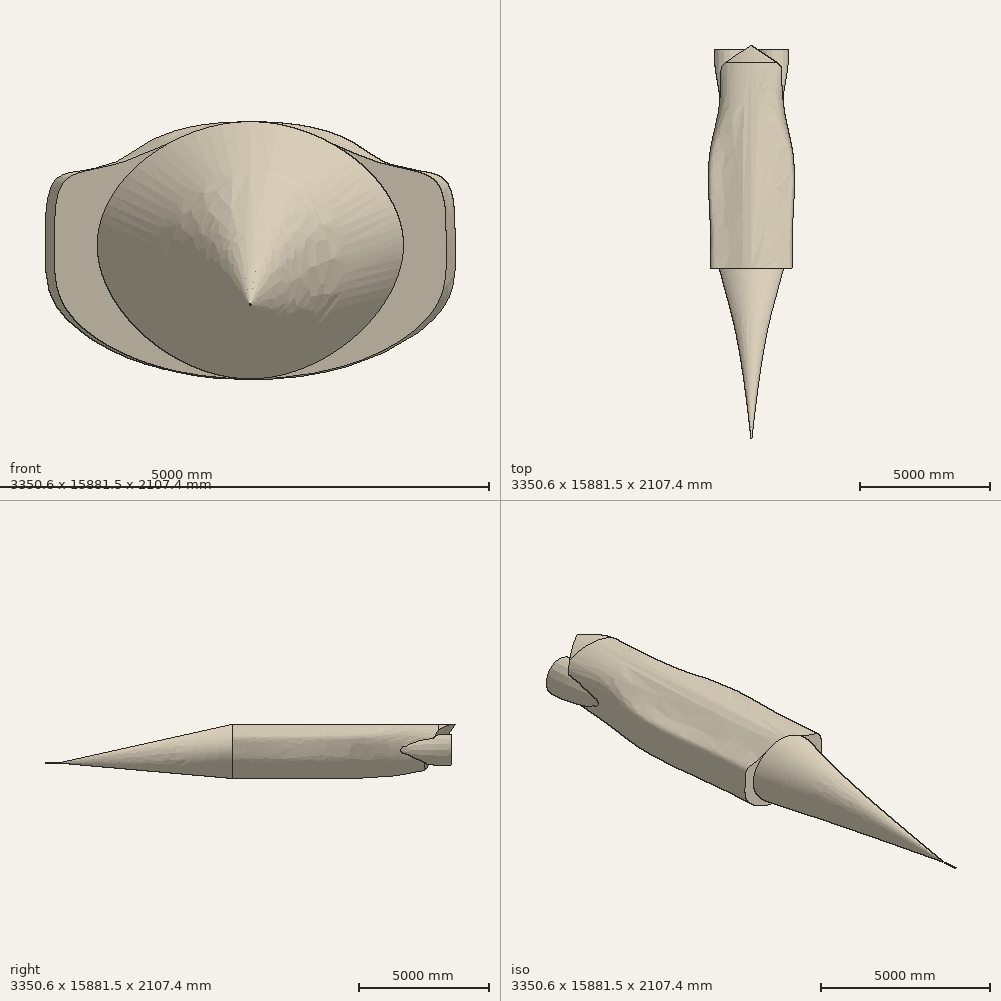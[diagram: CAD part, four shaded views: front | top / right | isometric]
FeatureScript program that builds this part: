
annotation { "Feature Type Name" : "Feature", "Feature Type Description" : "" }
export const myFeature = defineFeature(function(context is Context, id is Id, definition is map)
    precondition{}
    {
        {
            var Q0;
            Q0=qCreatedBy(makeId("Front.planeOp"),FACE);
            cPlane(context, id + "F0", {"entities" : qUnion([Q0]), "cplaneType" : CPlaneType.OFFSET, "offset" : 1750 * mm, "width" : 152.4 * mm, "height" : 152.4 * mm});
        }
        {
            var Q0;
            Q0=qCreatedBy(id+"F0.planeOp",FACE);
            var sketch = newSketch(context, id + "F1", { "sketchPlane" : qUnion([Q0])});
            skPoint(sketch, "E0.middle", {"position": v(0, 0) * mm});
            skFitSpline(sketch, "E1", {"points": [v(0, 1000) * mm, v(-1060, 662.5) * mm, v(-1517.6, 506.84) * mm, v(-1600, 0) * mm, v(-1517.6, -506.84) * mm, v(-750, -1000) * mm, v(750, -1000) * mm, v(1517.6, -506.84) * mm, v(1600, 0) * mm, v(1517.6, 506.84) * mm, v(1060, 662.5) * mm, v(0, 1000) * mm]});
            skSolve(sketch);
        }
        {
            var Q0;
            Q0=qCreatedBy(makeId("Front.planeOp"),FACE);
            var sketch = newSketch(context, id + "F2", { "sketchPlane" : qUnion([Q0])});
            skPoint(sketch, "E2.middle", {"position": v(0, 0) * mm});
            skFitSpline(sketch, "E3", {"points": [v(0, 1000) * mm, v(-1060, 662.5) * mm, v(-1517.6, 506.84) * mm, v(-1600, 0) * mm, v(-1517.6, -506.84) * mm, v(-750, -1000) * mm, v(750, -1000) * mm, v(1517.6, -506.84) * mm, v(1600, 0) * mm, v(1517.6, 506.84) * mm, v(1060, 662.5) * mm, v(0, 1000) * mm]});
            skSolve(sketch);
        }
        {
            var Q0;
            Q0=qCreatedBy(makeId("Front.planeOp"),FACE);
            cPlane(context, id + "F3", {"entities" : qUnion([Q0]), "cplaneType" : CPlaneType.OFFSET, "offset" : 2800 * mm, "oppositeDirection" : true, "width" : 150 * mm, "height" : 150 * mm});
        }
        {
            var Q0;
            Q0=qCreatedBy(id+"F3.planeOp",FACE);
            var sketch = newSketch(context, id + "F4", { "sketchPlane" : qUnion([Q0])});
            skPoint(sketch, "E4.middle", {"position": v(0, 0) * mm});
            skFitSpline(sketch, "E5", {"points": [v(0, 1000) * mm, v(-1060, 662.5) * mm, v(-1517.6, 506.84) * mm, v(-1600, 0) * mm, v(-1517.6, -506.84) * mm, v(-750, -1000) * mm, v(750, -1000) * mm, v(1517.6, -506.84) * mm, v(1600, 0) * mm, v(1517.6, 506.84) * mm, v(1060, 662.5) * mm, v(0, 1000) * mm]});
            skSolve(sketch);
        }
        {
            var Q0;
            Q0=qCreatedBy(makeId("Front.planeOp"),FACE);
            cPlane(context, id + "F5", {"entities" : qUnion([Q0]), "cplaneType" : CPlaneType.OFFSET, "offset" : 4500 * mm, "oppositeDirection" : true, "width" : 150 * mm, "height" : 150 * mm});
        }
        {
            var Q0;
            Q0=qCreatedBy(id+"F5.planeOp",FACE);
            var sketch = newSketch(context, id + "F6", { "sketchPlane" : qUnion([Q0])});
            skPoint(sketch, "E6.middle", {"position": v(0, 0) * mm});
            skFitSpline(sketch, "E7", {"points": [v(0, 1000) * mm, v(-1060, 662.5) * mm, v(-1250, 0) * mm, v(-1060, -662.5) * mm, v(0, -1000) * mm, v(1060, -662.5) * mm, v(1250, 0) * mm, v(1060, 662.5) * mm, v(0, 1000) * mm]});
            skSolve(sketch);
        }
        {
            var Q0;
            Q0=qCreatedBy(makeId("Front.planeOp"),FACE);
            cPlane(context, id + "F7", {"entities" : qUnion([Q0]), "cplaneType" : CPlaneType.OFFSET, "offset" : 6232.05 * mm, "oppositeDirection" : true, "width" : 150 * mm, "height" : 150 * mm});
        }
        {
            var Q0;
            Q0=qCreatedBy(id+"F7.planeOp",FACE);
            var sketch = newSketch(context, id + "F8", { "sketchPlane" : qUnion([Q0])});
            skPoint(sketch, "E8.middle", {"position": v(0, 0) * mm});
            skFitSpline(sketch, "E9", {"points": [v(0, 1000) * mm, v(-1060, 662.5) * mm, v(-1250, 0) * mm, v(-848, -530) * mm, v(848, -530) * mm, v(1250, 0) * mm, v(1060, 662.5) * mm, v(0, 1000) * mm]});
            skSolve(sketch);
        }
        {
            var Q0;
            Q0=makeQuery(id+"F1.imprint","IMPRINT",FACE,{"disambiguationData":[TD([[makeQuery(id+"F1.imprint","IMPRINT",EDGE,{"derivedFrom":sQuery(id+"F1.wireOp",EDGE,"E1")}),1.0]])]});
            var Q1;
            Q1=makeQuery(id+"F2.imprint","IMPRINT",FACE,{"disambiguationData":[TD([[makeQuery(id+"F2.imprint","IMPRINT",EDGE,{"derivedFrom":sQuery(id+"F2.wireOp",EDGE,"E3")}),1.0]])]});
            var Q2;
            Q2=makeQuery(id+"F4.imprint","IMPRINT",FACE,{"disambiguationData":[TD([[makeQuery(id+"F4.imprint","IMPRINT",EDGE,{"derivedFrom":sQuery(id+"F4.wireOp",EDGE,"E5")}),1.0]])]});
            var Q3;
            Q3=makeQuery(id+"F6.imprint","IMPRINT",FACE,{"disambiguationData":[TD([[makeQuery(id+"F6.imprint","IMPRINT",EDGE,{"derivedFrom":sQuery(id+"F6.wireOp",EDGE,"E7")}),1.0]])]});
            var Q4;
            Q4=makeQuery(id+"F8.imprint","IMPRINT",FACE,{"disambiguationData":[TD([[makeQuery(id+"F8.imprint","IMPRINT",EDGE,{"derivedFrom":sQuery(id+"F8.wireOp",EDGE,"E9")}),1.0]])]});
            loft(context, id + "F9", {"sheetProfilesArray" : [{ "sheetProfileEntities" : qUnion([Q0]) }, { "sheetProfileEntities" : qUnion([Q1]) }, { "sheetProfileEntities" : qUnion([Q2]) }, { "sheetProfileEntities" : qUnion([Q3]) }, { "sheetProfileEntities" : qUnion([Q4]) }]});
        }
        {
            var Q0;
            Q0=makeQuery(id+"F9.opLoft","CAP_FACE",FACE,{"disambiguationData":[OSD([makeQuery(id+"F8.imprint","IMPRINT",FACE,{"disambiguationData":[TD([[makeQuery(id+"F8.imprint","IMPRINT",EDGE,{"derivedFrom":sQuery(id+"F8.wireOp",EDGE,"E9")}),1.0]])]})])],"isStart":true});
            extrude(context, id + "F10", {"entities" : qUnion([Q0]), "operationType" : NewBodyOperationType.ADD, "depth" : 649.4 * mm, "offsetDistance" : 25 * mm});
        }
        {
            var Q0;
            Q0=qCreatedBy(makeId("Right.planeOp"),FACE);
            var sketch = newSketch(context, id + "F11", { "sketchPlane" : qUnion([Q0])});
            skLineSegment(sketch, "E10", {"start": v(0, 0) * mm, "end": v(4500, 0) * mm});
            skLineSegment(sketch, "E11", {"start": v(4500, 0) * mm, "end": v(6232.05, 0) * mm});
            skLineSegment(sketch, "E12", {"start": v(4500, 0) * mm, "end": v(4500, 1000) * mm});
            skLineSegment(sketch, "E13", {"start": v(4500, 1000) * mm, "end": v(6881.46, 1000) * mm});
            skLineSegment(sketch, "E14", {"start": v(6881.46, 1000) * mm, "end": v(6881.46, -1000) * mm});
            skLineSegment(sketch, "E15", {"start": v(6881.46, 1000) * mm, "end": v(6232.05, 0) * mm});
            skLineSegment(sketch, "E16", {"start": v(6232.05, 0) * mm, "end": v(5582.64, -1000) * mm});
            skLineSegment(sketch, "E17", {"start": v(5582.64, -1000) * mm, "end": v(6881.46, -1000) * mm});
            skSolve(sketch);
        }
        {
            var Q0;
            Q0=makeQuery(id+"F11.imprint","IMPRINT",FACE,{"disambiguationData":[TD([[makeQuery(id+"F11.imprint","IMPRINT",EDGE,{"derivedFrom":sQuery(id+"F11.wireOp",EDGE,"E14")}),-1.0]])]});
            var Q1;
            Q1=sQuery(id+"F11.wireOp",EDGE,"E13");
            revolve(context, id + "F12", {"operationType" : NewBodyOperationType.REMOVE, "entities" : qUnion([Q0]), "axis" : qUnion([Q1]), "revolveType" : RevolveType.SYMMETRIC, "oppositeDirection" : true, "angle" : 182 * degree});
        }
        {
            var Q0;
            Q0=qCreatedBy(id+"F0.planeOp",FACE);
            var sketch = newSketch(context, id + "F13", { "sketchPlane" : qUnion([Q0])});
            skFitSpline(sketch, "E18", {"points": [v(0, 1000) * mm, v(-1250, 0) * mm, v(0, -1099.92) * mm, v(1250, 0) * mm, v(0, 1000) * mm]});
            skSolve(sketch);
        }
        {
            var Q0;
            Q0=qCreatedBy(makeId("Front.planeOp"),FACE);
            cPlane(context, id + "F14", {"entities" : qUnion([Q0]), "cplaneType" : CPlaneType.OFFSET, "offset" : 3500 * mm, "width" : 150 * mm, "height" : 150 * mm});
        }
        {
            var Q0;
            Q0=qCreatedBy(id+"F14.planeOp",FACE);
            var sketch = newSketch(context, id + "F15", { "sketchPlane" : qUnion([Q0])});
            skCircle(sketch, "E19", {"center": v(0, -166.46) * mm, "radius": 777.75 * mm});
            skSolve(sketch);
        }
        {
            var Q0;
            Q0=qCreatedBy(makeId("Front.planeOp"),FACE);
            cPlane(context, id + "F16", {"entities" : qUnion([Q0]), "cplaneType" : CPlaneType.OFFSET, "offset" : 8450 * mm, "width" : 150 * mm, "height" : 150 * mm});
        }
        {
            var Q0;
            Q0=qCreatedBy(id+"F16.planeOp",FACE);
            var sketch = newSketch(context, id + "F17", { "sketchPlane" : qUnion([Q0])});
            skCircle(sketch, "E20", {"center": v(0, -495.98) * mm, "radius": 7.78 * mm});
            skSolve(sketch);
        }
        {
            var Q1;
            Q1=makeQuery(id+"F13.imprint","IMPRINT",FACE,{"disambiguationData":[TD([[makeQuery(id+"F13.imprint","IMPRINT",EDGE,{"derivedFrom":sQuery(id+"F13.wireOp",EDGE,"E18")}),1.0]])]});
            var Q2;
            Q2=makeQuery(id+"F15.imprint","IMPRINT",FACE,{"disambiguationData":[TD([[makeQuery(id+"F15.imprint","IMPRINT",EDGE,{"derivedFrom":sQuery(id+"F15.wireOp",EDGE,"E19")}),1.0]])]});
            var Q3;
            Q3=makeQuery(id+"F17.imprint","IMPRINT",FACE,{"disambiguationData":[TD([[makeQuery(id+"F17.imprint","IMPRINT",EDGE,{"derivedFrom":sQuery(id+"F17.wireOp",EDGE,"E20")}),1.0]])]});
            loft(context, id + "F18", {"operationType" : NewBodyOperationType.ADD, "sheetProfilesArray" : [{ "sheetProfileEntities" : qUnion([Q1]) }, { "sheetProfileEntities" : qUnion([Q2]) }, { "sheetProfileEntities" : qUnion([Q3]) }]});
        }
        {
            var Q0;
            Q0=makeQuery(id+"F18.opLoft","CAP_FACE",FACE,{"disambiguationData":[OSD([makeQuery(id+"F17.imprint","IMPRINT",FACE,{"disambiguationData":[TD([[makeQuery(id+"F17.imprint","IMPRINT",EDGE,{"derivedFrom":sQuery(id+"F17.wireOp",EDGE,"E20")}),1.0]])]})])],"isStart":true});
            extrude(context, id + "F19", {"entities" : qUnion([Q0]), "operationType" : NewBodyOperationType.ADD, "depth" : 550 * mm, "offsetDistance" : 25 * mm});
        }
        {
            var Q0;
            Q0=qCreatedBy(makeId("Front.planeOp"),FACE);
            cPlane(context, id + "F20", {"entities" : qUnion([Q0]), "cplaneType" : CPlaneType.OFFSET, "offset" : 3500 * mm, "oppositeDirection" : true, "width" : 150 * mm, "height" : 150 * mm});
        }
        {
            var Q0;
            Q0=qCreatedBy(id+"F20.planeOp",FACE);
            var sketch = newSketch(context, id + "F21", { "sketchPlane" : qUnion([Q0])});
            skCircle(sketch, "E21", {"center": v(-825, 0) * mm, "radius": 600 * mm});
            skCircle(sketch, "E22", {"center": v(825, 0) * mm, "radius": 600 * mm});
            skSolve(sketch);
        }
        {
            var Q0;
            Q0=qCreatedBy(makeId("Front.planeOp"),FACE);
            cPlane(context, id + "F22", {"entities" : qUnion([Q0]), "cplaneType" : CPlaneType.OFFSET, "offset" : 4500 * mm, "oppositeDirection" : true, "width" : 150 * mm, "height" : 150 * mm});
        }
        {
            var Q0;
            Q0=qCreatedBy(id+"F22.planeOp",FACE);
            var sketch = newSketch(context, id + "F23", { "sketchPlane" : qUnion([Q0])});
            skCircle(sketch, "E23", {"center": v(-825, 0) * mm, "radius": 400 * mm});
            skCircle(sketch, "E24", {"center": v(825, 0) * mm, "radius": 400 * mm});
            skSolve(sketch);
        }
        {
            var Q0;
            Q0=qCreatedBy(makeId("Front.planeOp"),FACE);
            cPlane(context, id + "F24", {"entities" : qUnion([Q0]), "cplaneType" : CPlaneType.OFFSET, "offset" : 6232.05 * mm, "oppositeDirection" : true, "width" : 150 * mm, "height" : 150 * mm});
        }
        {
            var Q0;
            Q0=qCreatedBy(id+"F24.planeOp",FACE);
            var sketch = newSketch(context, id + "F25", { "sketchPlane" : qUnion([Q0])});
            skCircle(sketch, "E25", {"center": v(-825, 0) * mm, "radius": 600 * mm});
            skCircle(sketch, "E26", {"center": v(825, 0) * mm, "radius": 600 * mm});
            skSolve(sketch);
        }
        {
            var Q0;
            Q0=qCreatedBy(makeId("Front.planeOp"),FACE);
            cPlane(context, id + "F26", {"entities" : qUnion([Q0]), "cplaneType" : CPlaneType.OFFSET, "offset" : 6732.05 * mm, "oppositeDirection" : true, "width" : 150 * mm, "height" : 150 * mm});
        }
        {
            var Q0;
            Q0=qCreatedBy(id+"F26.planeOp",FACE);
            var sketch = newSketch(context, id + "F27", { "sketchPlane" : qUnion([Q0])});
            skCircle(sketch, "E27", {"center": v(-825, 0) * mm, "radius": 600 * mm});
            skCircle(sketch, "E28", {"center": v(825, 0) * mm, "radius": 600 * mm});
            skSolve(sketch);
        }
        {
            var Q0;
            Q0=makeQuery(id+"F21.imprint","IMPRINT",FACE,{"disambiguationData":[TD([[makeQuery(id+"F21.imprint","IMPRINT",EDGE,{"derivedFrom":sQuery(id+"F21.wireOp",EDGE,"E21")}),1.0]])]});
            var Q1;
            Q1=makeQuery(id+"F23.imprint","IMPRINT",FACE,{"disambiguationData":[TD([[makeQuery(id+"F23.imprint","IMPRINT",EDGE,{"derivedFrom":sQuery(id+"F23.wireOp",EDGE,"E23")}),1.0]])]});
            var Q2;
            Q2=makeQuery(id+"F25.imprint","IMPRINT",FACE,{"disambiguationData":[TD([[makeQuery(id+"F25.imprint","IMPRINT",EDGE,{"derivedFrom":sQuery(id+"F25.wireOp",EDGE,"E25")}),1.0]])]});
            var Q3;
            Q3=makeQuery(id+"F27.imprint","IMPRINT",FACE,{"disambiguationData":[TD([[makeQuery(id+"F27.imprint","IMPRINT",EDGE,{"derivedFrom":sQuery(id+"F27.wireOp",EDGE,"E27")}),1.0]])]});
            loft(context, id + "F28", {"sheetProfilesArray" : [{ "sheetProfileEntities" : qUnion([Q0]) }, { "sheetProfileEntities" : qUnion([Q1]) }, { "sheetProfileEntities" : qUnion([Q2]) }, { "sheetProfileEntities" : qUnion([Q3]) }]});
        }
        {
            var Q0;
            Q0=makeQuery(id+"F21.imprint","IMPRINT",FACE,{"disambiguationData":[TD([[makeQuery(id+"F21.imprint","IMPRINT",EDGE,{"derivedFrom":sQuery(id+"F21.wireOp",EDGE,"E22")}),1.0]])]});
            var Q1;
            Q1=makeQuery(id+"F23.imprint","IMPRINT",FACE,{"disambiguationData":[TD([[makeQuery(id+"F23.imprint","IMPRINT",EDGE,{"derivedFrom":sQuery(id+"F23.wireOp",EDGE,"E24")}),1.0]])]});
            var Q2;
            Q2=makeQuery(id+"F25.imprint","IMPRINT",FACE,{"disambiguationData":[TD([[makeQuery(id+"F25.imprint","IMPRINT",EDGE,{"derivedFrom":sQuery(id+"F25.wireOp",EDGE,"E26")}),1.0]])]});
            var Q3;
            Q3=makeQuery(id+"F27.imprint","IMPRINT",FACE,{"disambiguationData":[TD([[makeQuery(id+"F27.imprint","IMPRINT",EDGE,{"derivedFrom":sQuery(id+"F27.wireOp",EDGE,"E28")}),1.0]])]});
            loft(context, id + "F29", {"sheetProfilesArray" : [{ "sheetProfileEntities" : qUnion([Q0]) }, { "sheetProfileEntities" : qUnion([Q1]) }, { "sheetProfileEntities" : qUnion([Q2]) }, { "sheetProfileEntities" : qUnion([Q3]) }]});
        }
    });
